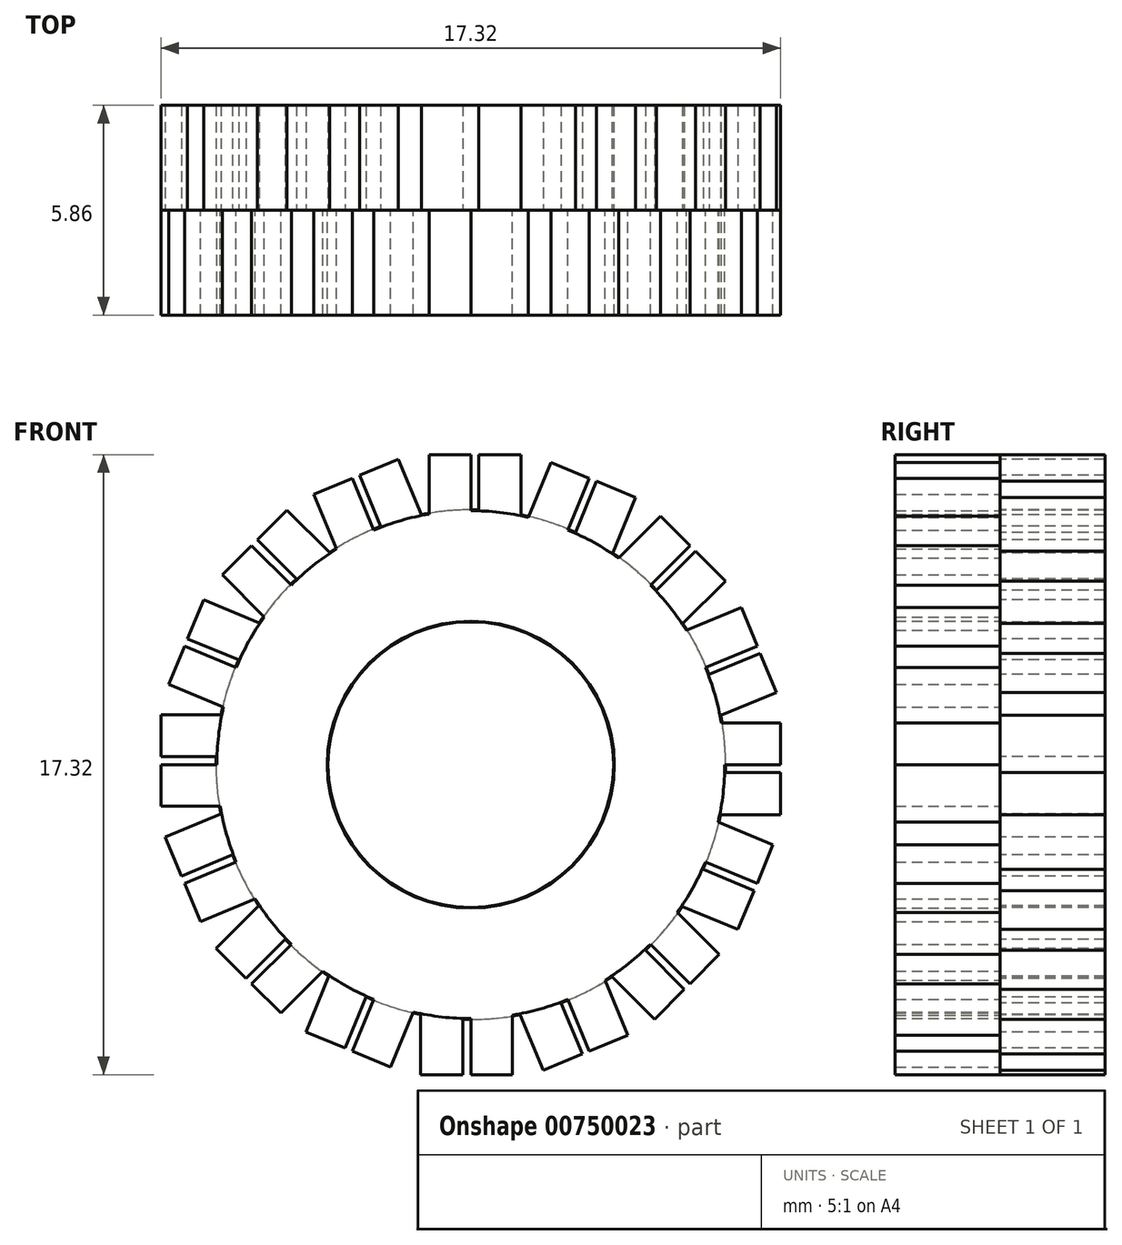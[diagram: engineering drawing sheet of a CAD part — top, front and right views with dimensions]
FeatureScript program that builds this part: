
annotation { "Feature Type Name" : "Feature", "Feature Type Description" : "" }
export const myFeature = defineFeature(function(context is Context, id is Id, definition is map)
    precondition{}
    {
        {
            var Q0;
            Q0=qCreatedBy(makeId("Front.planeOp"),FACE);
            var sketch = newSketch(context, id + "F0", { "sketchPlane" : qUnion([Q0])});
            skCircle(sketch, "E0", {"center": v(0, 0) * mm, "radius": 7.1 * mm});
            skCircle(sketch, "E1", {"center": v(0, 0) * mm, "radius": 4 * mm});
            skLineSegment(sketch, "E2.bottom", {"start": v(-1.16, 7) * mm, "end": v(0, 7) * mm});
            skLineSegment(sketch, "E2.top", {"start": v(-1.16, 8.66) * mm, "end": v(0, 8.66) * mm});
            skLineSegment(sketch, "E2.left", {"start": v(-1.16, 7) * mm, "end": v(-1.16, 8.66) * mm});
            skLineSegment(sketch, "E2.right", {"start": v(0, 7) * mm, "end": v(0, 8.66) * mm});
            skLineSegment(sketch, "E3.1.0", {"start": v(-4.39, 7.56) * mm, "end": v(-3.31, 8) * mm});
            skLineSegment(sketch, "E3.1.1", {"start": v(-3.75, 6.02) * mm, "end": v(-4.39, 7.56) * mm});
            skLineSegment(sketch, "E3.1.2", {"start": v(-2.68, 6.47) * mm, "end": v(-3.31, 8) * mm});
            skLineSegment(sketch, "E3.1.3", {"start": v(-3.75, 6.02) * mm, "end": v(-2.68, 6.47) * mm});
            skLineSegment(sketch, "E3.2.0", {"start": v(-6.94, 5.3) * mm, "end": v(-6.12, 6.12) * mm});
            skLineSegment(sketch, "E3.2.1", {"start": v(-5.77, 4.13) * mm, "end": v(-6.94, 5.3) * mm});
            skLineSegment(sketch, "E3.2.2", {"start": v(-4.95, 4.95) * mm, "end": v(-6.12, 6.12) * mm});
            skLineSegment(sketch, "E3.2.3", {"start": v(-5.77, 4.13) * mm, "end": v(-4.95, 4.95) * mm});
            skLineSegment(sketch, "E3.3.0", {"start": v(-8.44, 2.24) * mm, "end": v(-8, 3.31) * mm});
            skLineSegment(sketch, "E3.3.1", {"start": v(-6.91, 1.6) * mm, "end": v(-8.44, 2.24) * mm});
            skLineSegment(sketch, "E3.3.2", {"start": v(-6.47, 2.68) * mm, "end": v(-8, 3.31) * mm});
            skLineSegment(sketch, "E3.3.3", {"start": v(-6.91, 1.6) * mm, "end": v(-6.47, 2.68) * mm});
            skLineSegment(sketch, "E3.4.0", {"start": v(-8.66, -1.16) * mm, "end": v(-8.66, 0) * mm});
            skLineSegment(sketch, "E3.4.1", {"start": v(-7, -1.16) * mm, "end": v(-8.66, -1.16) * mm});
            skLineSegment(sketch, "E3.4.2", {"start": v(-7, 0) * mm, "end": v(-8.66, 0) * mm});
            skLineSegment(sketch, "E3.4.3", {"start": v(-7, -1.16) * mm, "end": v(-7, 0) * mm});
            skLineSegment(sketch, "E3.5.0", {"start": v(-7.56, -4.39) * mm, "end": v(-8, -3.31) * mm});
            skLineSegment(sketch, "E3.5.1", {"start": v(-6.02, -3.75) * mm, "end": v(-7.56, -4.39) * mm});
            skLineSegment(sketch, "E3.5.2", {"start": v(-6.47, -2.68) * mm, "end": v(-8, -3.31) * mm});
            skLineSegment(sketch, "E3.5.3", {"start": v(-6.02, -3.75) * mm, "end": v(-6.47, -2.68) * mm});
            skLineSegment(sketch, "E3.6.0", {"start": v(-5.3, -6.94) * mm, "end": v(-6.12, -6.12) * mm});
            skLineSegment(sketch, "E3.6.1", {"start": v(-4.13, -5.77) * mm, "end": v(-5.3, -6.94) * mm});
            skLineSegment(sketch, "E3.6.2", {"start": v(-4.95, -4.95) * mm, "end": v(-6.12, -6.12) * mm});
            skLineSegment(sketch, "E3.6.3", {"start": v(-4.13, -5.77) * mm, "end": v(-4.95, -4.95) * mm});
            skLineSegment(sketch, "E3.7.0", {"start": v(-2.24, -8.44) * mm, "end": v(-3.31, -8) * mm});
            skLineSegment(sketch, "E3.7.1", {"start": v(-1.6, -6.91) * mm, "end": v(-2.24, -8.44) * mm});
            skLineSegment(sketch, "E3.7.2", {"start": v(-2.68, -6.47) * mm, "end": v(-3.31, -8) * mm});
            skLineSegment(sketch, "E3.7.3", {"start": v(-1.6, -6.91) * mm, "end": v(-2.68, -6.47) * mm});
            skLineSegment(sketch, "E3.8.0", {"start": v(1.16, -8.66) * mm, "end": v(0, -8.66) * mm});
            skLineSegment(sketch, "E3.8.1", {"start": v(1.16, -7) * mm, "end": v(1.16, -8.66) * mm});
            skLineSegment(sketch, "E3.8.2", {"start": v(0, -7) * mm, "end": v(0, -8.66) * mm});
            skLineSegment(sketch, "E3.8.3", {"start": v(1.16, -7) * mm, "end": v(0, -7) * mm});
            skLineSegment(sketch, "E3.9.0", {"start": v(4.39, -7.56) * mm, "end": v(3.31, -8) * mm});
            skLineSegment(sketch, "E3.9.1", {"start": v(3.75, -6.02) * mm, "end": v(4.39, -7.56) * mm});
            skLineSegment(sketch, "E3.9.2", {"start": v(2.68, -6.47) * mm, "end": v(3.31, -8) * mm});
            skLineSegment(sketch, "E3.9.3", {"start": v(3.75, -6.02) * mm, "end": v(2.68, -6.47) * mm});
            skLineSegment(sketch, "E3.10.0", {"start": v(6.94, -5.3) * mm, "end": v(6.12, -6.12) * mm});
            skLineSegment(sketch, "E3.10.1", {"start": v(5.77, -4.13) * mm, "end": v(6.94, -5.3) * mm});
            skLineSegment(sketch, "E3.10.2", {"start": v(4.95, -4.95) * mm, "end": v(6.12, -6.12) * mm});
            skLineSegment(sketch, "E3.10.3", {"start": v(5.77, -4.13) * mm, "end": v(4.95, -4.95) * mm});
            skLineSegment(sketch, "E3.11.0", {"start": v(8.44, -2.24) * mm, "end": v(8, -3.31) * mm});
            skLineSegment(sketch, "E3.11.1", {"start": v(6.91, -1.6) * mm, "end": v(8.44, -2.24) * mm});
            skLineSegment(sketch, "E3.11.2", {"start": v(6.47, -2.68) * mm, "end": v(8, -3.31) * mm});
            skLineSegment(sketch, "E3.11.3", {"start": v(6.91, -1.6) * mm, "end": v(6.47, -2.68) * mm});
            skLineSegment(sketch, "E3.12.0", {"start": v(8.66, 1.16) * mm, "end": v(8.66, 0) * mm});
            skLineSegment(sketch, "E3.12.1", {"start": v(7, 1.16) * mm, "end": v(8.66, 1.16) * mm});
            skLineSegment(sketch, "E3.12.2", {"start": v(7, 0) * mm, "end": v(8.66, 0) * mm});
            skLineSegment(sketch, "E3.12.3", {"start": v(7, 1.16) * mm, "end": v(7, 0) * mm});
            skLineSegment(sketch, "E3.13.0", {"start": v(7.56, 4.39) * mm, "end": v(8, 3.31) * mm});
            skLineSegment(sketch, "E3.13.1", {"start": v(6.02, 3.75) * mm, "end": v(7.56, 4.39) * mm});
            skLineSegment(sketch, "E3.13.2", {"start": v(6.47, 2.68) * mm, "end": v(8, 3.31) * mm});
            skLineSegment(sketch, "E3.13.3", {"start": v(6.02, 3.75) * mm, "end": v(6.47, 2.68) * mm});
            skLineSegment(sketch, "E3.14.0", {"start": v(5.3, 6.94) * mm, "end": v(6.12, 6.12) * mm});
            skLineSegment(sketch, "E3.14.1", {"start": v(4.13, 5.77) * mm, "end": v(5.3, 6.94) * mm});
            skLineSegment(sketch, "E3.14.2", {"start": v(4.95, 4.95) * mm, "end": v(6.12, 6.12) * mm});
            skLineSegment(sketch, "E3.14.3", {"start": v(4.13, 5.77) * mm, "end": v(4.95, 4.95) * mm});
            skLineSegment(sketch, "E3.15.0", {"start": v(2.24, 8.44) * mm, "end": v(3.31, 8) * mm});
            skLineSegment(sketch, "E3.15.1", {"start": v(1.6, 6.91) * mm, "end": v(2.24, 8.44) * mm});
            skLineSegment(sketch, "E3.15.2", {"start": v(2.68, 6.47) * mm, "end": v(3.31, 8) * mm});
            skLineSegment(sketch, "E3.15.3", {"start": v(1.6, 6.91) * mm, "end": v(2.68, 6.47) * mm});
            skSolve(sketch);
        }
        {
            var Q0;
            Q0 = qSketchRegion(id + "F0", true);
            extrude(context, id + "F1", {"entities" : qUnion([Q0]), "depth" : 2.93 * mm, "offsetDistance" : 25 * mm});
        }
        {
            var Q0;
            Q0=makeQuery(id+"F1.opExtrude","CAP_FACE",FACE,{"disambiguationData":[OSD([sQuery(id+"F0.wireOp",EDGE,"E0"),sQuery(id+"F0.wireOp",EDGE,"E1"),sQuery(id+"F0.wireOp",EDGE,"E2.top"),sQuery(id+"F0.wireOp",EDGE,"E2.left"),sQuery(id+"F0.wireOp",EDGE,"E2.right"),sQuery(id+"F0.wireOp",EDGE,"E3.1.0"),sQuery(id+"F0.wireOp",EDGE,"E3.1.1"),sQuery(id+"F0.wireOp",EDGE,"E3.1.2"),sQuery(id+"F0.wireOp",EDGE,"E3.2.0"),sQuery(id+"F0.wireOp",EDGE,"E3.2.1"),sQuery(id+"F0.wireOp",EDGE,"E3.2.2"),sQuery(id+"F0.wireOp",EDGE,"E3.3.0"),sQuery(id+"F0.wireOp",EDGE,"E3.3.1"),sQuery(id+"F0.wireOp",EDGE,"E3.3.2"),sQuery(id+"F0.wireOp",EDGE,"E3.4.0"),sQuery(id+"F0.wireOp",EDGE,"E3.4.1"),sQuery(id+"F0.wireOp",EDGE,"E3.4.2"),sQuery(id+"F0.wireOp",EDGE,"E3.5.0"),sQuery(id+"F0.wireOp",EDGE,"E3.5.1"),sQuery(id+"F0.wireOp",EDGE,"E3.5.2"),sQuery(id+"F0.wireOp",EDGE,"E3.6.0"),sQuery(id+"F0.wireOp",EDGE,"E3.6.1"),sQuery(id+"F0.wireOp",EDGE,"E3.6.2"),sQuery(id+"F0.wireOp",EDGE,"E3.7.0"),sQuery(id+"F0.wireOp",EDGE,"E3.7.1"),sQuery(id+"F0.wireOp",EDGE,"E3.7.2"),sQuery(id+"F0.wireOp",EDGE,"E3.8.0"),sQuery(id+"F0.wireOp",EDGE,"E3.8.1"),sQuery(id+"F0.wireOp",EDGE,"E3.8.2"),sQuery(id+"F0.wireOp",EDGE,"E3.9.0"),sQuery(id+"F0.wireOp",EDGE,"E3.9.1"),sQuery(id+"F0.wireOp",EDGE,"E3.9.2"),sQuery(id+"F0.wireOp",EDGE,"E3.10.0"),sQuery(id+"F0.wireOp",EDGE,"E3.10.1"),sQuery(id+"F0.wireOp",EDGE,"E3.10.2"),sQuery(id+"F0.wireOp",EDGE,"E3.11.0"),sQuery(id+"F0.wireOp",EDGE,"E3.11.1"),sQuery(id+"F0.wireOp",EDGE,"E3.11.2"),sQuery(id+"F0.wireOp",EDGE,"E3.12.0"),sQuery(id+"F0.wireOp",EDGE,"E3.12.1"),sQuery(id+"F0.wireOp",EDGE,"E3.12.2"),sQuery(id+"F0.wireOp",EDGE,"E3.13.0"),sQuery(id+"F0.wireOp",EDGE,"E3.13.1"),sQuery(id+"F0.wireOp",EDGE,"E3.13.2"),sQuery(id+"F0.wireOp",EDGE,"E3.14.0"),sQuery(id+"F0.wireOp",EDGE,"E3.14.1"),sQuery(id+"F0.wireOp",EDGE,"E3.14.2"),sQuery(id+"F0.wireOp",EDGE,"E3.15.0"),sQuery(id+"F0.wireOp",EDGE,"E3.15.1"),sQuery(id+"F0.wireOp",EDGE,"E3.15.2")])],"isStart":true});
            var sketch = newSketch(context, id + "F2", { "sketchPlane" : qUnion([Q0])});
            skCircle(sketch, "E4", {"center": v(0, 0) * mm, "radius": 3.99 * mm});
            skCircle(sketch, "E5", {"center": v(0, 0) * mm, "radius": 7.12 * mm});
            skLineSegment(sketch, "E6.bottom", {"start": v(-1.4, 6.96) * mm, "end": v(-0.22, 6.96) * mm});
            skLineSegment(sketch, "E6.top", {"start": v(-1.4, 8.66) * mm, "end": v(-0.22, 8.66) * mm});
            skLineSegment(sketch, "E6.left", {"start": v(-1.4, 6.96) * mm, "end": v(-1.4, 8.66) * mm});
            skLineSegment(sketch, "E6.right", {"start": v(-0.22, 6.96) * mm, "end": v(-0.22, 8.66) * mm});
            skLineSegment(sketch, "E7.1.0", {"start": v(-4.6, 7.46) * mm, "end": v(-3.52, 7.92) * mm});
            skLineSegment(sketch, "E7.1.1", {"start": v(-3.95, 5.9) * mm, "end": v(-4.6, 7.46) * mm});
            skLineSegment(sketch, "E7.1.2", {"start": v(-3.95, 5.9) * mm, "end": v(-2.86, 6.34) * mm});
            skLineSegment(sketch, "E7.1.3", {"start": v(-2.86, 6.34) * mm, "end": v(-3.52, 7.92) * mm});
            skLineSegment(sketch, "E7.2.0", {"start": v(-7.11, 5.13) * mm, "end": v(-6.28, 5.97) * mm});
            skLineSegment(sketch, "E7.2.1", {"start": v(-5.9, 3.93) * mm, "end": v(-7.11, 5.13) * mm});
            skLineSegment(sketch, "E7.2.2", {"start": v(-5.9, 3.93) * mm, "end": v(-5.07, 4.76) * mm});
            skLineSegment(sketch, "E7.2.3", {"start": v(-5.07, 4.76) * mm, "end": v(-6.28, 5.97) * mm});
            skLineSegment(sketch, "E7.3.0", {"start": v(-8.54, 2.02) * mm, "end": v(-8.08, 3.11) * mm});
            skLineSegment(sketch, "E7.3.1", {"start": v(-6.96, 1.37) * mm, "end": v(-8.54, 2.02) * mm});
            skLineSegment(sketch, "E7.3.2", {"start": v(-6.96, 1.37) * mm, "end": v(-6.51, 2.46) * mm});
            skLineSegment(sketch, "E7.3.3", {"start": v(-6.51, 2.46) * mm, "end": v(-8.08, 3.11) * mm});
            skLineSegment(sketch, "E7.4.0", {"start": v(-8.66, -1.4) * mm, "end": v(-8.66, -0.22) * mm});
            skLineSegment(sketch, "E7.4.1", {"start": v(-6.96, -1.4) * mm, "end": v(-8.66, -1.4) * mm});
            skLineSegment(sketch, "E7.4.2", {"start": v(-6.96, -1.4) * mm, "end": v(-6.96, -0.22) * mm});
            skLineSegment(sketch, "E7.4.3", {"start": v(-6.96, -0.22) * mm, "end": v(-8.66, -0.22) * mm});
            skLineSegment(sketch, "E7.5.0", {"start": v(-7.46, -4.6) * mm, "end": v(-7.92, -3.52) * mm});
            skLineSegment(sketch, "E7.5.1", {"start": v(-5.9, -3.95) * mm, "end": v(-7.46, -4.6) * mm});
            skLineSegment(sketch, "E7.5.2", {"start": v(-5.9, -3.95) * mm, "end": v(-6.34, -2.86) * mm});
            skLineSegment(sketch, "E7.5.3", {"start": v(-6.34, -2.86) * mm, "end": v(-7.92, -3.52) * mm});
            skLineSegment(sketch, "E7.6.0", {"start": v(-5.13, -7.11) * mm, "end": v(-5.97, -6.28) * mm});
            skLineSegment(sketch, "E7.6.1", {"start": v(-3.93, -5.9) * mm, "end": v(-5.13, -7.11) * mm});
            skLineSegment(sketch, "E7.6.2", {"start": v(-3.93, -5.9) * mm, "end": v(-4.76, -5.07) * mm});
            skLineSegment(sketch, "E7.6.3", {"start": v(-4.76, -5.07) * mm, "end": v(-5.97, -6.28) * mm});
            skLineSegment(sketch, "E7.7.0", {"start": v(-2.02, -8.54) * mm, "end": v(-3.11, -8.08) * mm});
            skLineSegment(sketch, "E7.7.1", {"start": v(-1.37, -6.96) * mm, "end": v(-2.02, -8.54) * mm});
            skLineSegment(sketch, "E7.7.2", {"start": v(-1.37, -6.96) * mm, "end": v(-2.46, -6.51) * mm});
            skLineSegment(sketch, "E7.7.3", {"start": v(-2.46, -6.51) * mm, "end": v(-3.11, -8.08) * mm});
            skLineSegment(sketch, "E7.8.0", {"start": v(1.4, -8.66) * mm, "end": v(0.22, -8.66) * mm});
            skLineSegment(sketch, "E7.8.1", {"start": v(1.4, -6.96) * mm, "end": v(1.4, -8.66) * mm});
            skLineSegment(sketch, "E7.8.2", {"start": v(1.4, -6.96) * mm, "end": v(0.22, -6.96) * mm});
            skLineSegment(sketch, "E7.8.3", {"start": v(0.22, -6.96) * mm, "end": v(0.22, -8.66) * mm});
            skLineSegment(sketch, "E7.9.0", {"start": v(4.6, -7.46) * mm, "end": v(3.52, -7.92) * mm});
            skLineSegment(sketch, "E7.9.1", {"start": v(3.95, -5.9) * mm, "end": v(4.6, -7.46) * mm});
            skLineSegment(sketch, "E7.9.2", {"start": v(3.95, -5.9) * mm, "end": v(2.86, -6.34) * mm});
            skLineSegment(sketch, "E7.9.3", {"start": v(2.86, -6.34) * mm, "end": v(3.52, -7.92) * mm});
            skLineSegment(sketch, "E7.10.0", {"start": v(7.11, -5.13) * mm, "end": v(6.28, -5.97) * mm});
            skLineSegment(sketch, "E7.10.1", {"start": v(5.9, -3.93) * mm, "end": v(7.11, -5.13) * mm});
            skLineSegment(sketch, "E7.10.2", {"start": v(5.9, -3.93) * mm, "end": v(5.07, -4.76) * mm});
            skLineSegment(sketch, "E7.10.3", {"start": v(5.07, -4.76) * mm, "end": v(6.28, -5.97) * mm});
            skLineSegment(sketch, "E7.11.0", {"start": v(8.54, -2.02) * mm, "end": v(8.08, -3.11) * mm});
            skLineSegment(sketch, "E7.11.1", {"start": v(6.96, -1.37) * mm, "end": v(8.54, -2.02) * mm});
            skLineSegment(sketch, "E7.11.2", {"start": v(6.96, -1.37) * mm, "end": v(6.51, -2.46) * mm});
            skLineSegment(sketch, "E7.11.3", {"start": v(6.51, -2.46) * mm, "end": v(8.08, -3.11) * mm});
            skLineSegment(sketch, "E7.12.0", {"start": v(8.66, 1.4) * mm, "end": v(8.66, 0.22) * mm});
            skLineSegment(sketch, "E7.12.1", {"start": v(6.96, 1.4) * mm, "end": v(8.66, 1.4) * mm});
            skLineSegment(sketch, "E7.12.2", {"start": v(6.96, 1.4) * mm, "end": v(6.96, 0.22) * mm});
            skLineSegment(sketch, "E7.12.3", {"start": v(6.96, 0.22) * mm, "end": v(8.66, 0.22) * mm});
            skLineSegment(sketch, "E7.13.0", {"start": v(7.46, 4.6) * mm, "end": v(7.92, 3.52) * mm});
            skLineSegment(sketch, "E7.13.1", {"start": v(5.9, 3.95) * mm, "end": v(7.46, 4.6) * mm});
            skLineSegment(sketch, "E7.13.2", {"start": v(5.9, 3.95) * mm, "end": v(6.34, 2.86) * mm});
            skLineSegment(sketch, "E7.13.3", {"start": v(6.34, 2.86) * mm, "end": v(7.92, 3.52) * mm});
            skLineSegment(sketch, "E7.14.0", {"start": v(5.13, 7.11) * mm, "end": v(5.97, 6.28) * mm});
            skLineSegment(sketch, "E7.14.1", {"start": v(3.93, 5.9) * mm, "end": v(5.13, 7.11) * mm});
            skLineSegment(sketch, "E7.14.2", {"start": v(3.93, 5.9) * mm, "end": v(4.76, 5.07) * mm});
            skLineSegment(sketch, "E7.14.3", {"start": v(4.76, 5.07) * mm, "end": v(5.97, 6.28) * mm});
            skLineSegment(sketch, "E7.15.0", {"start": v(2.02, 8.54) * mm, "end": v(3.11, 8.08) * mm});
            skLineSegment(sketch, "E7.15.1", {"start": v(1.37, 6.96) * mm, "end": v(2.02, 8.54) * mm});
            skLineSegment(sketch, "E7.15.2", {"start": v(1.37, 6.96) * mm, "end": v(2.46, 6.51) * mm});
            skLineSegment(sketch, "E7.15.3", {"start": v(2.46, 6.51) * mm, "end": v(3.11, 8.08) * mm});
            skSolve(sketch);
        }
        {
            var Q0;
            Q0 = qSketchRegion(id + "F2", true);
            extrude(context, id + "F3", {"entities" : qUnion([Q0]), "operationType" : NewBodyOperationType.ADD, "depth" : 2.93 * mm, "offsetDistance" : 25 * mm});
        }
    });
